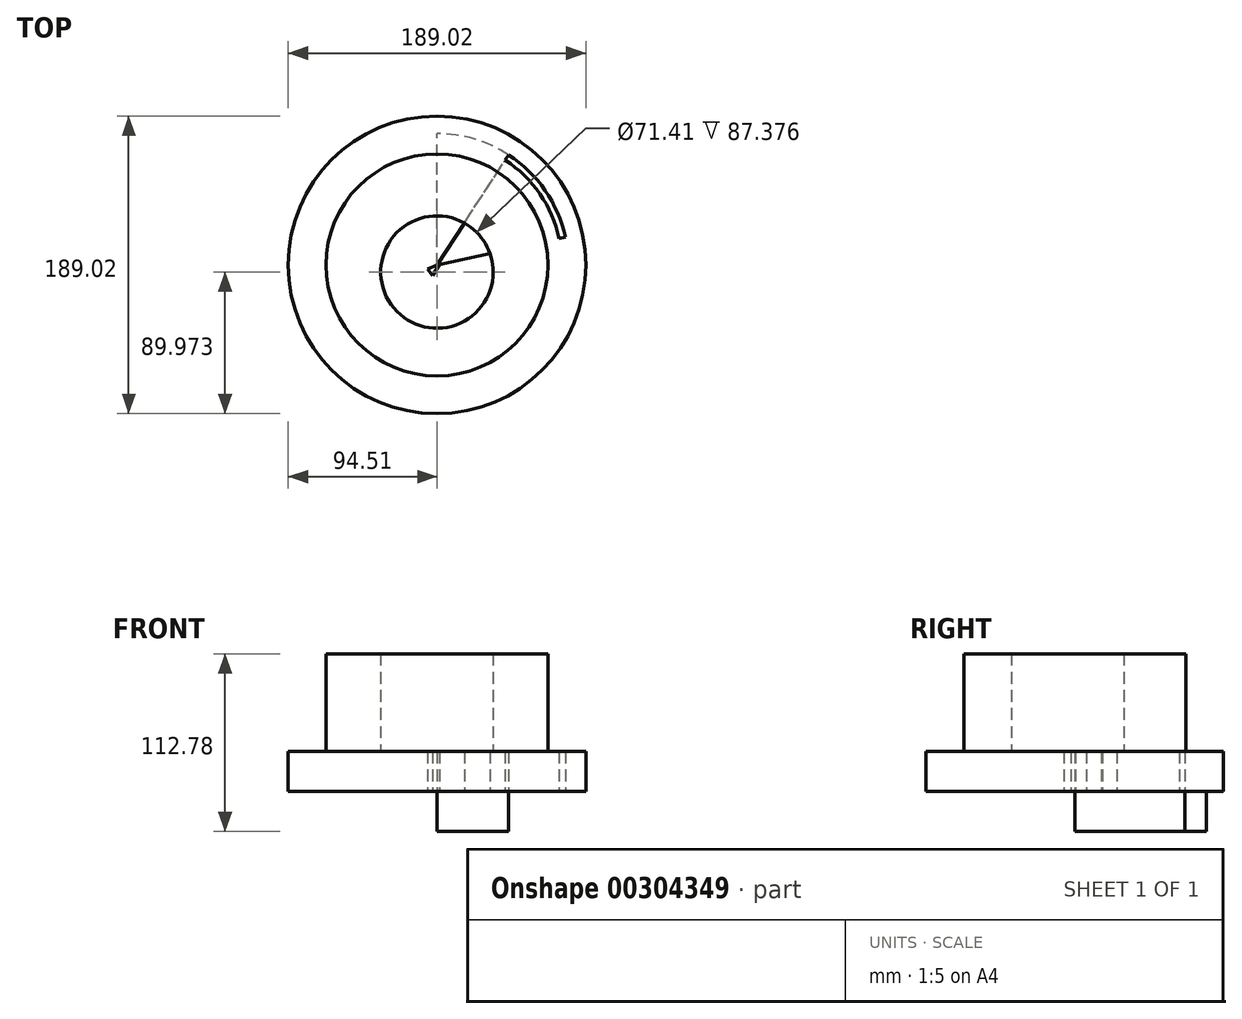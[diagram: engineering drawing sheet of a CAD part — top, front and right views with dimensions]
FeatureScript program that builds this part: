
annotation { "Feature Type Name" : "Feature", "Feature Type Description" : "" }
export const myFeature = defineFeature(function(context is Context, id is Id, definition is map)
    precondition{}
    {
        {
            var Q0;
            Q0=qCreatedBy(makeId("Top.planeOp"),FACE);
            var sketch = newSketch(context, id + "F0", { "sketchPlane" : qUnion([Q0])});
            skCircle(sketch, "E0", {"center": v(0, 0) * mm, "radius": 94.51 * mm});
            skCircle(sketch, "E1", {"center": v(0, 0) * mm, "radius": 83.4 * mm});
            skLineSegment(sketch, "E2", {"start": v(0, 0) * mm, "end": v(25.43, -79.43) * mm});
            skLineSegment(sketch, "E3", {"start": v(0, 0) * mm, "end": v(74.76, -36.98) * mm});
            skLineSegment(sketch, "E4", {"start": v(0, 0) * mm, "end": v(-31.3, -77.31) * mm});
            skLineSegment(sketch, "E5", {"start": v(0, 0) * mm, "end": v(81.52, 17.63) * mm});
            skLineSegment(sketch, "E6", {"start": v(81.52, 17.63) * mm, "end": v(0, 0) * mm});
            skLineSegment(sketch, "E7", {"start": v(0, 0) * mm, "end": v(45.53, 69.88) * mm});
            skLineSegment(sketch, "E8", {"start": v(45.53, 69.88) * mm, "end": v(-2.76, -6.82) * mm});
            skLineSegment(sketch, "E9", {"start": v(0, 0) * mm, "end": v(-76.86, -32.39) * mm});
            skLineSegment(sketch, "E10", {"start": v(0, 0) * mm, "end": v(0, 83.4) * mm});
            skLineSegment(sketch, "E11", {"start": v(-2.76, -6.82) * mm, "end": v(-56.8, 61.07) * mm});
            skSolve(sketch);
        }
        {
            var Q0;
            {var subQ0=sQuery(id+"F0.wireOp",EDGE,"E2");var subQ1=sQuery(id+"F0.wireOp",EDGE,"E1");var subQ2=makeQuery(id+"F0.imprint","INTERSECT",VERTEX,{"derivedFrom":[subQ1,subQ0]});Q0=makeQuery(id+"F0.imprint","IMPRINT",FACE,{"disambiguationData":[TD([[makeQuery(id+"F0.imprint","IMPRINT",EDGE,{"disambiguationData":[TD([[subQ2,-1.0]])],"derivedFrom":subQ1}),1.0]])]});}
            var Q1;
            Q1=makeQuery(id+"F0.imprint","IMPRINT",FACE,{"disambiguationData":[TD([[makeQuery(id+"F0.imprint","IMPRINT",EDGE,{"derivedFrom":sQuery(id+"F0.wireOp",EDGE,"E0")}),1.0]])]});
            var Q2;
            {var subQ0=sQuery(id+"F0.wireOp",EDGE,"E2");var subQ1=sQuery(id+"F0.wireOp",EDGE,"E1");var subQ2=makeQuery(id+"F0.imprint","INTERSECT",VERTEX,{"derivedFrom":[subQ1,subQ0]});Q2=makeQuery(id+"F0.imprint","IMPRINT",FACE,{"disambiguationData":[TD([[makeQuery(id+"F0.imprint","IMPRINT",EDGE,{"disambiguationData":[TD([[subQ2,1.0]])],"derivedFrom":subQ1}),1.0]])]});}
            var Q3;
            {var subQ0=sQuery(id+"F0.wireOp",EDGE,"E4");var subQ1=sQuery(id+"F0.wireOp",EDGE,"E1");var subQ2=makeQuery(id+"F0.imprint","INTERSECT",VERTEX,{"derivedFrom":[subQ1,subQ0]});Q3=makeQuery(id+"F0.imprint","IMPRINT",FACE,{"disambiguationData":[TD([[makeQuery(id+"F0.imprint","IMPRINT",EDGE,{"disambiguationData":[TD([[subQ2,1.0]])],"derivedFrom":subQ1}),1.0]])]});}
            var Q4;
            {var subQ0=sQuery(id+"F0.wireOp",EDGE,"E9");var subQ1=sQuery(id+"F0.wireOp",EDGE,"E1");var subQ2=makeQuery(id+"F0.imprint","INTERSECT",VERTEX,{"derivedFrom":[subQ1,subQ0]});Q4=makeQuery(id+"F0.imprint","IMPRINT",FACE,{"disambiguationData":[TD([[makeQuery(id+"F0.imprint","IMPRINT",EDGE,{"disambiguationData":[TD([[subQ2,1.0]])],"derivedFrom":subQ1}),1.0]])]});}
            var Q5;
            {var subQ0=sQuery(id+"F0.wireOp",EDGE,"E10");Q5=makeQuery(id+"F0.imprint","IMPRINT",FACE,{"disambiguationData":[TD([[makeQuery(id+"F0.imprint","IMPRINT",EDGE,{"derivedFrom":subQ0}),1.0]])]});}
            var Q6;
            {var subQ0=sQuery(id+"F0.wireOp",EDGE,"E7");Q6=makeQuery(id+"F0.imprint","IMPRINT",FACE,{"disambiguationData":[TD([[makeQuery(id+"F0.imprint","IMPRINT",EDGE,{"derivedFrom":subQ0}),1.0]])]});}
            var Q7;
            {var subQ0=sQuery(id+"F0.wireOp",EDGE,"E6");var subQ1=sQuery(id+"F0.wireOp",EDGE,"E1");var subQ2=makeQuery(id+"F0.imprint","INTERSECT",VERTEX,{"derivedFrom":[subQ1,subQ0]});Q7=makeQuery(id+"F0.imprint","IMPRINT",FACE,{"disambiguationData":[TD([[makeQuery(id+"F0.imprint","IMPRINT",EDGE,{"disambiguationData":[TD([[subQ2,-1.0]])],"derivedFrom":subQ0}),-1.0]])]});}
            var Q8;
            {var subQ0=sQuery(id+"F0.wireOp",EDGE,"E3");var subQ1=sQuery(id+"F0.wireOp",EDGE,"E1");var subQ2=makeQuery(id+"F0.imprint","INTERSECT",VERTEX,{"derivedFrom":[subQ1,subQ0]});Q8=makeQuery(id+"F0.imprint","IMPRINT",FACE,{"disambiguationData":[TD([[makeQuery(id+"F0.imprint","IMPRINT",EDGE,{"disambiguationData":[TD([[subQ2,-1.0]])],"derivedFrom":subQ1}),1.0]])]});}
            extrude(context, id + "F1", {"entities" : qUnion([Q0, Q1, Q2, Q3, Q4, Q5, Q6, Q7, Q8]), "depth" : 25.4 * mm});
        }
        {
            var Q0;
            {var subQ0=sQuery(id+"F0.wireOp",EDGE,"E7");Q0=makeQuery(id+"F0.imprint","IMPRINT",FACE,{"disambiguationData":[TD([[makeQuery(id+"F0.imprint","IMPRINT",EDGE,{"derivedFrom":subQ0}),1.0]])]});}
            extrude(context, id + "F2", {"entities" : qUnion([Q0]), "operationType" : NewBodyOperationType.ADD, "oppositeDirection" : true, "depth" : 25.4 * mm});
        }
        {
            var Q0;
            {var subQ0=sQuery(id+"F0.wireOp",EDGE,"E10");Q0=makeQuery(id+"F0.imprint","IMPRINT",FACE,{"disambiguationData":[TD([[makeQuery(id+"F0.imprint","IMPRINT",EDGE,{"derivedFrom":subQ0}),1.0]])]});}
            var Q1;
            {var subQ0=sQuery(id+"F0.wireOp",EDGE,"E9");var subQ1=sQuery(id+"F0.wireOp",EDGE,"E1");var subQ2=makeQuery(id+"F0.imprint","INTERSECT",VERTEX,{"derivedFrom":[subQ1,subQ0]});Q1=makeQuery(id+"F0.imprint","IMPRINT",FACE,{"disambiguationData":[TD([[makeQuery(id+"F0.imprint","IMPRINT",EDGE,{"disambiguationData":[TD([[subQ2,1.0]])],"derivedFrom":subQ1}),1.0]])]});}
            var Q2;
            {var subQ0=sQuery(id+"F0.wireOp",EDGE,"E4");var subQ1=sQuery(id+"F0.wireOp",EDGE,"E1");var subQ2=makeQuery(id+"F0.imprint","INTERSECT",VERTEX,{"derivedFrom":[subQ1,subQ0]});Q2=makeQuery(id+"F0.imprint","IMPRINT",FACE,{"disambiguationData":[TD([[makeQuery(id+"F0.imprint","IMPRINT",EDGE,{"disambiguationData":[TD([[subQ2,1.0]])],"derivedFrom":subQ1}),1.0]])]});}
            var Q3;
            {var subQ0=sQuery(id+"F0.wireOp",EDGE,"E2");var subQ1=sQuery(id+"F0.wireOp",EDGE,"E1");var subQ2=makeQuery(id+"F0.imprint","INTERSECT",VERTEX,{"derivedFrom":[subQ1,subQ0]});Q3=makeQuery(id+"F0.imprint","IMPRINT",FACE,{"disambiguationData":[TD([[makeQuery(id+"F0.imprint","IMPRINT",EDGE,{"disambiguationData":[TD([[subQ2,1.0]])],"derivedFrom":subQ1}),1.0]])]});}
            var Q4;
            {var subQ0=sQuery(id+"F0.wireOp",EDGE,"E2");var subQ1=sQuery(id+"F0.wireOp",EDGE,"E1");var subQ2=makeQuery(id+"F0.imprint","INTERSECT",VERTEX,{"derivedFrom":[subQ1,subQ0]});Q4=makeQuery(id+"F0.imprint","IMPRINT",FACE,{"disambiguationData":[TD([[makeQuery(id+"F0.imprint","IMPRINT",EDGE,{"disambiguationData":[TD([[subQ2,-1.0]])],"derivedFrom":subQ1}),1.0]])]});}
            var Q5;
            {var subQ0=sQuery(id+"F0.wireOp",EDGE,"E3");var subQ1=sQuery(id+"F0.wireOp",EDGE,"E1");var subQ2=makeQuery(id+"F0.imprint","INTERSECT",VERTEX,{"derivedFrom":[subQ1,subQ0]});Q5=makeQuery(id+"F0.imprint","IMPRINT",FACE,{"disambiguationData":[TD([[makeQuery(id+"F0.imprint","IMPRINT",EDGE,{"disambiguationData":[TD([[subQ2,-1.0]])],"derivedFrom":subQ1}),1.0]])]});}
            var Q6;
            {var subQ0=sQuery(id+"F0.wireOp",EDGE,"E6");var subQ1=sQuery(id+"F0.wireOp",EDGE,"E1");var subQ2=makeQuery(id+"F0.imprint","INTERSECT",VERTEX,{"derivedFrom":[subQ1,subQ0]});Q6=makeQuery(id+"F0.imprint","IMPRINT",FACE,{"disambiguationData":[TD([[makeQuery(id+"F0.imprint","IMPRINT",EDGE,{"disambiguationData":[TD([[subQ2,-1.0]])],"derivedFrom":subQ0}),-1.0]])]});}
            var Q7;
            {var subQ0=sQuery(id+"F0.wireOp",EDGE,"E7");Q7=makeQuery(id+"F0.imprint","IMPRINT",FACE,{"disambiguationData":[TD([[makeQuery(id+"F0.imprint","IMPRINT",EDGE,{"derivedFrom":subQ0}),1.0]])]});}
            extrude(context, id + "F3", {"entities" : qUnion([Q0, Q1, Q2, Q3, Q4, Q5, Q6, Q7]), "depth" : 25.4 * mm});
        }
        {
            var Q0;
            Q0=qCreatedBy(makeId("Top.planeOp"),FACE);
            var sketch = newSketch(context, id + "F4", { "sketchPlane" : qUnion([Q0])});
            skCircle(sketch, "E12", {"center": v(0, 0) * mm, "radius": 79.4 * mm});
            skCircle(sketch, "E13", {"center": v(0, 0) * mm, "radius": 70.52 * mm});
            skCircle(sketch, "E14", {"center": v(0, -4.54) * mm, "radius": 35.7 * mm});
            skSolve(sketch);
        }
        {
            var Q0;
            Q0=makeQuery(id+"F4.imprint","IMPRINT",FACE,{"disambiguationData":[TD([[makeQuery(id+"F4.imprint","IMPRINT",EDGE,{"derivedFrom":sQuery(id+"F4.wireOp",EDGE,"E13")}),1.0]])]});
            extrude(context, id + "F5", {"entities" : qUnion([Q0]), "depth" : 87.38 * mm});
        }
        {
            var Q0;
            Q0=makeQuery(id+"F4.imprint","IMPRINT",FACE,{"disambiguationData":[TD([[makeQuery(id+"F4.imprint","IMPRINT",EDGE,{"derivedFrom":sQuery(id+"F4.wireOp",EDGE,"E12")}),1.0]])]});
            extrude(context, id + "F6", {"entities" : qUnion([Q0]), "operationType" : NewBodyOperationType.ADD, "depth" : 25.4 * mm});
        }
    });
